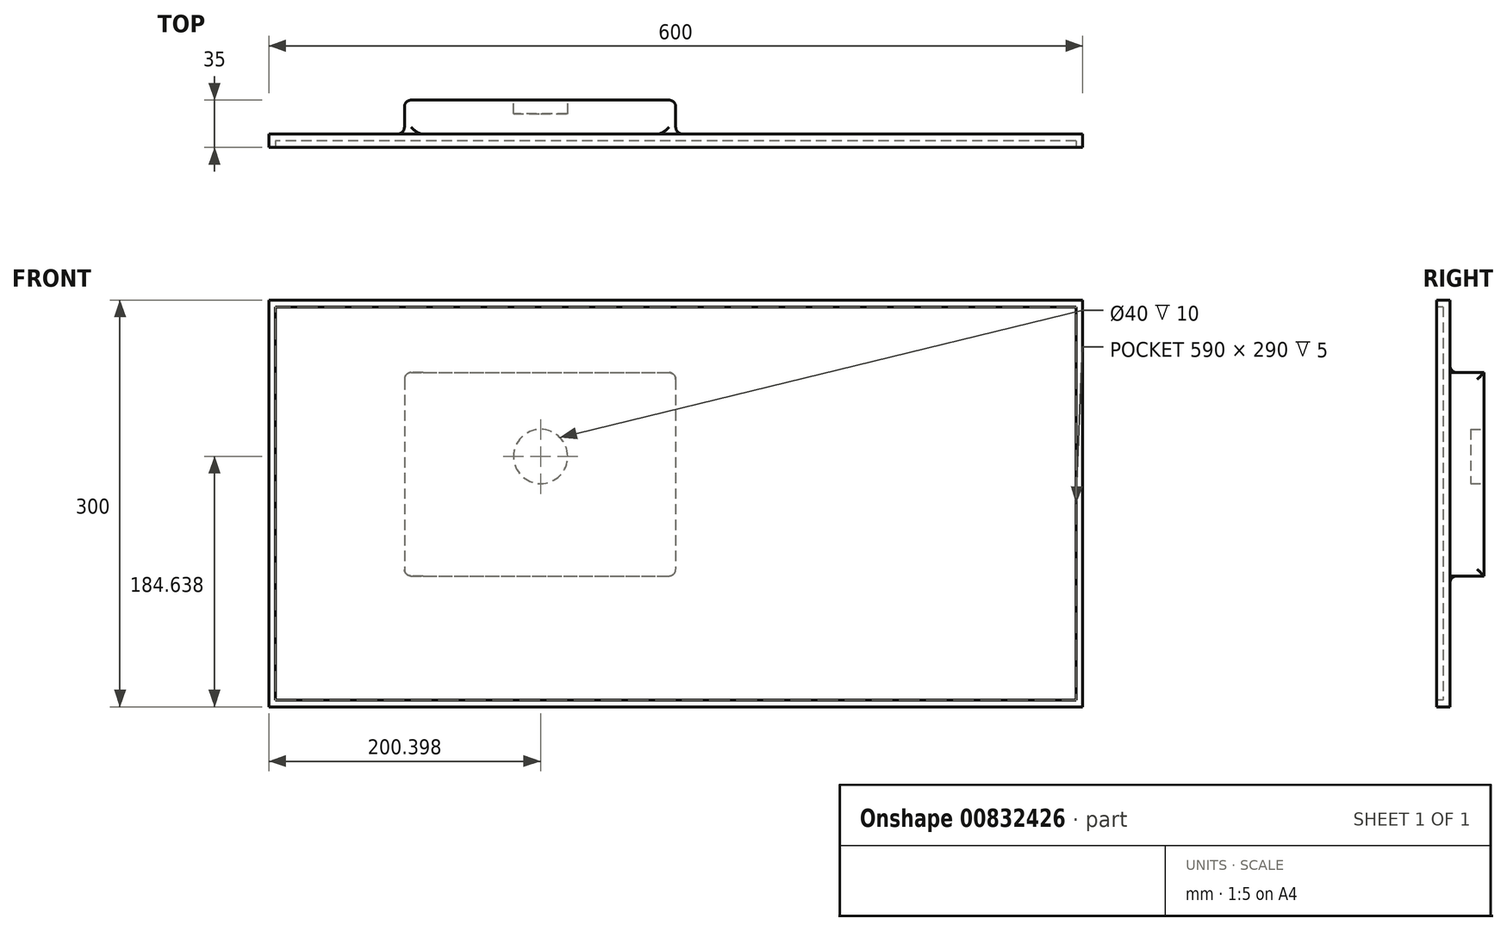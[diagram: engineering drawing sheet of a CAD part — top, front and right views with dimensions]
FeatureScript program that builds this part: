
annotation { "Feature Type Name" : "Feature", "Feature Type Description" : "" }
export const myFeature = defineFeature(function(context is Context, id is Id, definition is map)
    precondition{}
    {
        {
            var Q0;
            Q0=qCreatedBy(makeId("Front.planeOp"),FACE);
            var sketch = newSketch(context, id + "F0", { "sketchPlane" : qUnion([Q0])});
            skLineSegment(sketch, "E0.bottom", {"start": v(-400, 253.48) * mm, "end": v(200, 253.48) * mm});
            skLineSegment(sketch, "E0.top", {"start": v(-400, -46.52) * mm, "end": v(200, -46.52) * mm});
            skLineSegment(sketch, "E0.left", {"start": v(-400, 253.48) * mm, "end": v(-400, -46.52) * mm});
            skLineSegment(sketch, "E0.right", {"start": v(200, 253.48) * mm, "end": v(200, -46.52) * mm});
            skSolve(sketch);
        }
        {
            var Q0;
            Q0=makeQuery(id+"F0.imprint","IMPRINT",FACE,{"disambiguationData":[TD([[makeQuery(id+"F0.imprint","IMPRINT",EDGE,{"derivedFrom":sQuery(id+"F0.wireOp",EDGE,"E0.bottom")}),-1.0]])]});
            extrude(context, id + "F1", {"entities" : qUnion([Q0]), "depth" : 10 * mm, "offsetDistance" : 25 * mm});
        }
        {
            var Q0;
            Q0=makeQuery(id+"F1.opExtrude","CAP_FACE",FACE,{"disambiguationData":[OSD([sQuery(id+"F0.wireOp",EDGE,"E0.bottom"),sQuery(id+"F0.wireOp",EDGE,"E0.top"),sQuery(id+"F0.wireOp",EDGE,"E0.left"),sQuery(id+"F0.wireOp",EDGE,"E0.right")])],"isStart":false});
            var sketch = newSketch(context, id + "F2", { "sketchPlane" : qUnion([Q0])});
            skLineSegment(sketch, "E1.0", {"start": v(-395, 248.48) * mm, "end": v(-395, -41.52) * mm});
            skLineSegment(sketch, "E1.1", {"start": v(195, 248.48) * mm, "end": v(-395, 248.48) * mm});
            skLineSegment(sketch, "E1.2", {"start": v(195, -41.52) * mm, "end": v(195, 248.48) * mm});
            skLineSegment(sketch, "E1.3", {"start": v(-395, -41.52) * mm, "end": v(195, -41.52) * mm});
            skSolve(sketch);
        }
        {
            var Q0;
            Q0=makeQuery(id+"F2.imprint","IMPRINT",FACE,{"disambiguationData":[TD([[makeQuery(id+"F2.imprint","IMPRINT",EDGE,{"derivedFrom":sQuery(id+"F2.wireOp",EDGE,"E1.0")}),1.0]])]});
            extrude(context, id + "F3", {"entities" : qUnion([Q0]), "operationType" : NewBodyOperationType.REMOVE, "oppositeDirection" : true, "depth" : 5 * mm, "offsetDistance" : 25 * mm});
        }
        {
            var Q0;
            Q0=makeQuery(id+"F3.boolean.opBoolean","COPY",FACE,{"derivedFrom":makeQuery(id+"F3.opExtrude","CAP_FACE",FACE,{"disambiguationData":[OSD([sQuery(id+"F2.wireOp",EDGE,"E1.0"),sQuery(id+"F2.wireOp",EDGE,"E1.1"),sQuery(id+"F2.wireOp",EDGE,"E1.2"),sQuery(id+"F2.wireOp",EDGE,"E1.3")])],"isStart":false})});
            var sketch = newSketch(context, id + "F4", { "sketchPlane" : qUnion([Q0])});
            skLineSegment(sketch, "E2.bottom", {"start": v(-300, 200) * mm, "end": v(-100, 200) * mm});
            skLineSegment(sketch, "E2.top", {"start": v(-300, 50) * mm, "end": v(-100, 50) * mm});
            skLineSegment(sketch, "E2.left", {"start": v(-300, 200) * mm, "end": v(-300, 50) * mm});
            skLineSegment(sketch, "E2.right", {"start": v(-100, 200) * mm, "end": v(-100, 50) * mm});
            skSolve(sketch);
        }
        {
            var Q0;
            Q0=makeQuery(id+"F4.imprint","IMPRINT",FACE,{"disambiguationData":[TD([[makeQuery(id+"F4.imprint","IMPRINT",EDGE,{"derivedFrom":sQuery(id+"F4.wireOp",EDGE,"E2.bottom")}),-1.0]])]});
            extrude(context, id + "F5", {"entities" : qUnion([Q0]), "operationType" : NewBodyOperationType.ADD, "oppositeDirection" : true, "depth" : 30 * mm, "offsetDistance" : 25 * mm});
        }
        {
            var Q0;
            Q0=makeQuery(id+"F5.opExtrude","SWEPT_FACE",FACE,{"disambiguationData":[OSD([sQuery(id+"F4.wireOp",EDGE,"E2.right")])]});
            var Q1;
            Q1=makeQuery(id+"F5.opExtrude","SWEPT_FACE",FACE,{"disambiguationData":[OSD([sQuery(id+"F4.wireOp",EDGE,"E2.left")])]});
            fillet(context, id + "F6", {"entities" : qUnion([Q0, Q1]), "radius" : 5 * mm, "tangentPropagation" : true, "allowEdgeOverflow" : false});
        }
        {
            var Q0;
            Q0=makeQuery(id+"F5.opExtrude","CAP_FACE",FACE,{"disambiguationData":[OSD([sQuery(id+"F4.wireOp",EDGE,"E2.bottom"),sQuery(id+"F4.wireOp",EDGE,"E2.top"),sQuery(id+"F4.wireOp",EDGE,"E2.left"),sQuery(id+"F4.wireOp",EDGE,"E2.right")])],"isStart":false});
            var sketch = newSketch(context, id + "F7", { "sketchPlane" : qUnion([Q0])});
            skCircle(sketch, "E3", {"center": v(199.6, 138.12) * mm, "radius": 20 * mm});
            skSolve(sketch);
        }
        {
            var Q0;
            Q0=makeQuery(id+"F7.imprint","IMPRINT",FACE,{"disambiguationData":[TD([[makeQuery(id+"F7.imprint","IMPRINT",EDGE,{"derivedFrom":sQuery(id+"F7.wireOp",EDGE,"E3")}),1.0]])]});
            extrude(context, id + "F8", {"entities" : qUnion([Q0]), "operationType" : NewBodyOperationType.REMOVE, "oppositeDirection" : true, "depth" : 10 * mm, "offsetDistance" : 25 * mm});
        }
    });
